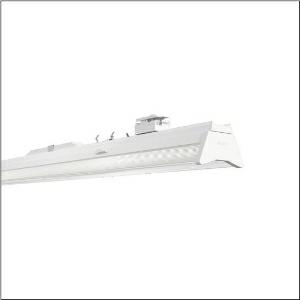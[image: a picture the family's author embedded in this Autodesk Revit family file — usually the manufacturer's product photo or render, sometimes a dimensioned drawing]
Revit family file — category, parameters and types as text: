
# Revit family: licross_r__21_performance_mo_52tm16dn445g_a9c4
name_source: partatom
category: Lighting Fixtures
units: mm (PartAtom-declared; Revit-internal decimal feet)

## family parameters
Cut with Voids When Loaded = No
Host = Face
Light Source = No
Part Type = Normal
Room Calculation Point = No
Round Connector Dimension = Use Diameter
Shared = No

## types (1)
- --- (1 x LED, 4500 lm, 24.9 W, 4000K)
    Apparent Load = 25 VA
    CIE Flux Codes = 66 88 96 79 100
    Color Rendering = 80
    Color Temperature = 4000K
    Default Elevation = 1800 mm
    Description = Licross® 21 Performance MO, luminaire insert, of sheet steel, galvanised, coil coated, white, length: 1.500mm, width: 120mm, height: 123mm, LED rated luminous flux: 4.500lm, light colour: 840, control gear: DALI 2, with plug, 5-pole, with phase selection, mains connection: 220..240V, AC, 50/60Hz, rated input power: 25W, halogen-free wiring, primary light control with lens, of plastic, primary optical cover: cover, of PMMA, CAT 2 (L<= 3000cd/m²), light emission: direct/indirect distribution, primary light characteristic: symmetric, protection rating (complete): IP40, insulation class (complete): insulation class I (protective earthing), certification: CE, ENEC, UKCA, protection symbol: D if used in an environment without relevant dust loads with corresponding accessories, impact resistance: IK06, permissible ambient temperature for indoor applications: -25..+50°C, corresponds to IFS (International Featured Standards) requirements for safety and quality in the food industry, reducing of maximum allowable ambient temperature of 5°C with ceiling mounting, LABS conformity tested according to VDMA 24364:2018-05, packaging unit: 1 piece
    Height = 114 mm
    Lamp = 1 x LED
    Lamp Light Flux = 4500 lm
    Lamp Power = 24.9 W
    Lamp count = 1
    Length = 1500 mm
    Luminous efficacy = 181 lm/W
    Manufacturer = Siteco
    ModVariant = No
    Model = 52TM16DN445G
    Mounting Place = Ceiling
    Mounting Type = Pendant
    Number of Poles = 1
    OnlyDefault = Yes
    Power Factor = 1
    Product Name = Licross® 21 Performance MO
    Product group = luminaire insert
    ProductGroupID = 902
    Protection Class = Protection class I
    Protection Degree = IP 40
    RLX_Detail_Level = 1
    RLX_Emergency_Light_Flux = 0 lm
    RLX_Emergency_Type = 0
    RLX_Emergency_Type_DB = No
    RlxData = <blob elided: 33581 chars, md5=239fd243>
    Socket = socket
    Standby Power = 0 W
    System Light Flux = 4500 lm
    System Power = 25 W
    Type Comments = factory setting: luminous flux: 100 % | dim-lin: 254 | 165 mA
    Type Image = l_1256138.jpg
    URL = http://relux.com
    VarID = @adj_049320
    Voltage = 0 V
    Weight = 0.00 kg
    Width = 120 mm

## geometry (parser evidence)
native form markers: Blend x4, Sweep x13
no freeform markers — native parametric forms only
